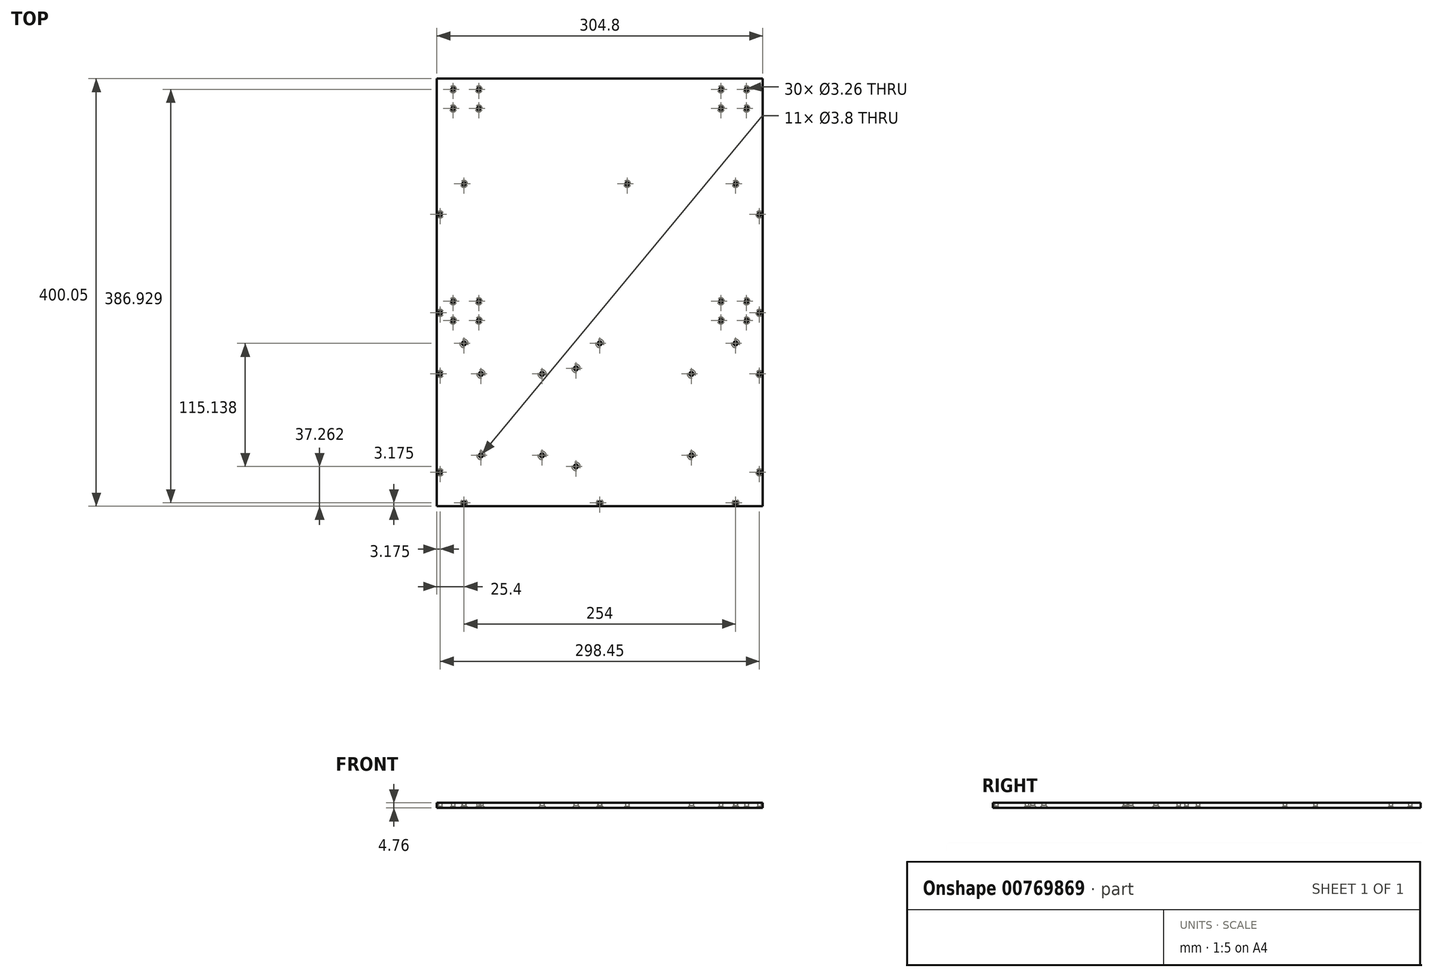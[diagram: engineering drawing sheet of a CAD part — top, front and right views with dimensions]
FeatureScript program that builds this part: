
annotation { "Feature Type Name" : "Feature", "Feature Type Description" : "" }
export const myFeature = defineFeature(function(context is Context, id is Id, definition is map)
    precondition{}
    {
        {
            var Q0;
            Q0=qCreatedBy(makeId("Top.planeOp"),FACE);
            var sketch = newSketch(context, id + "F0", { "sketchPlane" : qUnion([Q0])});
            skLineSegment(sketch, "E0.bottom", {"start": v(-152.4, 152.4) * mm, "end": v(152.4, 152.4) * mm});
            skLineSegment(sketch, "E0.top", {"start": v(-152.4, -152.4) * mm, "end": v(152.4, -152.4) * mm});
            skLineSegment(sketch, "E0.left", {"start": v(-152.4, 152.4) * mm, "end": v(-152.4, -152.4) * mm});
            skLineSegment(sketch, "E0.right", {"start": v(152.4, 152.4) * mm, "end": v(152.4, -152.4) * mm});
            skLineSegment(sketch, "E1", {"start": v(-152.4, 152.4) * mm, "end": v(152.4, -152.4) * mm, "construction": true});
            skSolve(sketch);
        }
        {
            var Q0;
            Q0 = qSketchRegion(id + "F0", true);
            extrude(context, id + "F1", {"entities" : qUnion([Q0]), "depth" : 4.76 * mm, "offsetDistance" : 25.4 * mm});
        }
        {
            var Q0;
            Q0=makeQuery(id+"F1.opExtrude","CAP_FACE",FACE,{"disambiguationData":[OSD([sQuery(id+"F0.wireOp",EDGE,"E0.bottom"),sQuery(id+"F0.wireOp",EDGE,"E0.top"),sQuery(id+"F0.wireOp",EDGE,"E0.left"),sQuery(id+"F0.wireOp",EDGE,"E0.right")])],"isStart":true});
            var sketch = newSketch(context, id + "F2", { "sketchPlane" : qUnion([Q0])});
            skLineSegment(sketch, "E2", {"start": v(-152.4, 0) * mm, "end": v(152.4, 0) * mm, "construction": true});
            skPoint(sketch, "E3", {"position": v(-127, 0) * mm});
            skPoint(sketch, "E4", {"position": v(0, 0) * mm});
            skPoint(sketch, "E5", {"position": v(127, 0) * mm});
            skSolve(sketch);
        }
        {
            var Q0;
            Q0=sQuery(id+"F2.wireOp",VERTEX,"E3");
            var Q1;
            Q1=sQuery(id+"F2.wireOp",VERTEX,"E4");
            var Q2;
            Q2=sQuery(id+"F2.wireOp",VERTEX,"E5");
            var Q3;
            Q3=makeQuery(id+"F1.opExtrude","SWEPT_BODY",BODY,{"disambiguationData":[OSD([sQuery(id+"F0.wireOp",EDGE,"E0.bottom"),sQuery(id+"F0.wireOp",EDGE,"E0.top"),sQuery(id+"F0.wireOp",EDGE,"E0.left"),sQuery(id+"F0.wireOp",EDGE,"E0.right")])]});
            hole(context, id + "F3", {"style" : HoleStyle.C_SINK, "endStyle" : HoleEndStyle.THROUGH, "standardTappedOrClearance" : lookupTablePath({ "standard" : "ANSI", "fit" : "Normal (ASME)", "size" : "#6", "type" : "Clearance" }), "standardBlindInLast" : lookupTablePath({ "fit" : "Free", "standard" : "ANSI", "size" : "#6", "type" : "Clearance" }), "holeDiameter" : 3.8 * mm, "cSinkDiameter" : 7.8 * mm, "cSinkAngle" : 82 * degree, "majorDiameter" : 6.35 * mm, "isTappedThrough" : true, "tappedDepth" : 7.77 * mm, "tapClearance" : 3, "locations" : qUnion([Q0, Q1, Q2]), "scope" : qUnion([Q3])});
        }
        {
            var Q0;
            Q0=makeQuery(id+"F1.opExtrude","CAP_FACE",FACE,{"disambiguationData":[OSD([sQuery(id+"F0.wireOp",EDGE,"E0.bottom"),sQuery(id+"F0.wireOp",EDGE,"E0.top"),sQuery(id+"F0.wireOp",EDGE,"E0.left"),sQuery(id+"F0.wireOp",EDGE,"E0.right")])],"isStart":false});
            var sketch = newSketch(context, id + "F4", { "sketchPlane" : qUnion([Q0])});
            skLineSegment(sketch, "E6.bottom", {"start": v(-152.4, 152.4) * mm, "end": v(152.4, 152.4) * mm});
            skLineSegment(sketch, "E6.top", {"start": v(-152.4, 247.65) * mm, "end": v(152.4, 247.65) * mm});
            skLineSegment(sketch, "E6.left", {"start": v(-152.4, 152.4) * mm, "end": v(-152.4, 247.65) * mm});
            skLineSegment(sketch, "E6.right", {"start": v(152.4, 152.4) * mm, "end": v(152.4, 247.65) * mm});
            skSolve(sketch);
        }
        {
            var Q0;
            Q0 = qSketchRegion(id + "F4", true);
            extrude(context, id + "F5", {"entities" : qUnion([Q0]), "operationType" : NewBodyOperationType.ADD, "oppositeDirection" : true, "depth" : 4.76 * mm, "offsetDistance" : 25.4 * mm});
        }
        {
            var Q0;
            Q0=makeQuery(id+"F5.boolean.opBoolean","MERGE",FACE,{"derivedFrom":[makeQuery(id+"F1.opExtrude","CAP_FACE",FACE,{"disambiguationData":[OSD([sQuery(id+"F0.wireOp",EDGE,"E0.bottom"),sQuery(id+"F0.wireOp",EDGE,"E0.top"),sQuery(id+"F0.wireOp",EDGE,"E0.left"),sQuery(id+"F0.wireOp",EDGE,"E0.right")])],"isStart":true}),makeQuery(id+"F5.opExtrude","CAP_FACE",FACE,{"disambiguationData":[OSD([sQuery(id+"F4.wireOp",EDGE,"E6.bottom"),sQuery(id+"F4.wireOp",EDGE,"E6.top"),sQuery(id+"F4.wireOp",EDGE,"E6.left"),sQuery(id+"F4.wireOp",EDGE,"E6.right")])],"isStart":false})]});
            var sketch = newSketch(context, id + "F6", { "sketchPlane" : qUnion([Q0])});
            skLineSegment(sketch, "E7", {"start": v(152.4, 149.23) * mm, "end": v(-152.4, 149.23) * mm, "construction": true});
            skPoint(sketch, "E8", {"position": v(127, 149.23) * mm});
            skPoint(sketch, "E9", {"position": v(0, 149.23) * mm});
            skPoint(sketch, "E10", {"position": v(-127, 149.23) * mm});
            skLineSegment(sketch, "E11", {"start": v(-152.4, -149.23) * mm, "end": v(152.4, -149.23) * mm, "construction": true});
            skPoint(sketch, "E12", {"position": v(-127, -149.23) * mm});
            skPoint(sketch, "E13", {"position": v(25.58, -149.23) * mm});
            skPoint(sketch, "E14", {"position": v(127, -149.23) * mm});
            skLineSegment(sketch, "E15", {"start": v(149.22, -247.65) * mm, "end": v(149.22, 152.4) * mm, "construction": true});
            skLineSegment(sketch, "E16", {"start": v(-149.22, -247.65) * mm, "end": v(-149.23, 152.4) * mm, "construction": true});
            skPoint(sketch, "E17", {"position": v(-149.23, -28.57) * mm});
            skPoint(sketch, "E18", {"position": v(-149.22, -120.65) * mm});
            skPoint(sketch, "E19", {"position": v(-149.23, 28.58) * mm});
            skPoint(sketch, "E20", {"position": v(-149.23, 120.65) * mm});
            skPoint(sketch, "E21", {"position": v(149.22, 120.65) * mm});
            skPoint(sketch, "E22", {"position": v(149.22, 28.58) * mm});
            skPoint(sketch, "E23", {"position": v(149.22, -28.57) * mm});
            skPoint(sketch, "E24", {"position": v(149.22, -120.65) * mm});
            skSolve(sketch);
        }
        {
            var Q0;
            Q0=sQuery(id+"F6.wireOp",VERTEX,"E8");
            var Q1;
            Q1=sQuery(id+"F6.wireOp",VERTEX,"E9");
            var Q2;
            Q2=sQuery(id+"F6.wireOp",VERTEX,"E10");
            var Q3;
            Q3=sQuery(id+"F6.wireOp",VERTEX,"E12");
            var Q4;
            Q4=sQuery(id+"F6.wireOp",VERTEX,"E13");
            var Q5;
            Q5=sQuery(id+"F6.wireOp",VERTEX,"E14");
            var Q6;
            Q6=sQuery(id+"F6.wireOp",VERTEX,"E24");
            var Q7;
            Q7=sQuery(id+"F6.wireOp",VERTEX,"E22");
            var Q8;
            Q8=sQuery(id+"F6.wireOp",VERTEX,"E21");
            var Q9;
            Q9=sQuery(id+"F6.wireOp",VERTEX,"E20");
            var Q10;
            Q10=sQuery(id+"F6.wireOp",VERTEX,"E19");
            var Q11;
            Q11=sQuery(id+"F6.wireOp",VERTEX,"E17");
            var Q12;
            Q12=sQuery(id+"F6.wireOp",VERTEX,"E18");
            var Q13;
            Q13=sQuery(id+"F6.wireOp",VERTEX,"E23");
            var Q14;
            Q14=makeQuery(id+"F1.opExtrude","SWEPT_BODY",BODY,{"disambiguationData":[OSD([sQuery(id+"F0.wireOp",EDGE,"E0.bottom"),sQuery(id+"F0.wireOp",EDGE,"E0.top"),sQuery(id+"F0.wireOp",EDGE,"E0.left"),sQuery(id+"F0.wireOp",EDGE,"E0.right")])]});
            hole(context, id + "F7", {"style" : HoleStyle.C_SINK, "endStyle" : HoleEndStyle.BLIND, "standardTappedOrClearance" : lookupTablePath({ "standard" : "ANSI", "fit" : "Normal (ASME)", "size" : "#4", "type" : "Clearance" }), "standardBlindInLast" : lookupTablePath({ "fit" : "Free", "standard" : "ANSI", "size" : "#4", "type" : "Clearance" }), "holeDiameter" : 3.26 * mm, "cSinkDiameter" : 6.48 * mm, "cSinkAngle" : 82 * degree, "majorDiameter" : 2.84 * mm, "holeDepth" : 13.74 * mm, "tappedDepth" : 11.84 * mm, "tapClearance" : 3, "locations" : qUnion([Q0, Q1, Q2, Q3, Q4, Q5, Q6, Q7, Q8, Q9, Q10, Q11, Q12, Q13]), "scope" : qUnion([Q14])});
        }
        {
            var Q0;
            Q0=makeQuery(id+"F5.boolean.opBoolean","MERGE",FACE,{"derivedFrom":[makeQuery(id+"F1.opExtrude","CAP_FACE",FACE,{"disambiguationData":[OSD([sQuery(id+"F0.wireOp",EDGE,"E0.bottom"),sQuery(id+"F0.wireOp",EDGE,"E0.top"),sQuery(id+"F0.wireOp",EDGE,"E0.left"),sQuery(id+"F0.wireOp",EDGE,"E0.right")])],"isStart":true}),makeQuery(id+"F5.opExtrude","CAP_FACE",FACE,{"disambiguationData":[OSD([sQuery(id+"F4.wireOp",EDGE,"E6.bottom"),sQuery(id+"F4.wireOp",EDGE,"E6.top"),sQuery(id+"F4.wireOp",EDGE,"E6.left"),sQuery(id+"F4.wireOp",EDGE,"E6.right")])],"isStart":false})]});
            var sketch = newSketch(context, id + "F8", { "sketchPlane" : qUnion([Q0])});
            skLineSegment(sketch, "E25.bottom", {"start": v(137.24, -237.7) * mm, "end": v(113.24, -237.7) * mm, "construction": true});
            skLineSegment(sketch, "E25.top", {"start": v(137.24, -219.7) * mm, "end": v(113.24, -219.7) * mm, "construction": true});
            skLineSegment(sketch, "E25.left", {"start": v(137.24, -237.7) * mm, "end": v(137.24, -219.7) * mm, "construction": true});
            skLineSegment(sketch, "E25.right", {"start": v(113.24, -237.7) * mm, "end": v(113.24, -219.7) * mm, "construction": true});
            skLineSegment(sketch, "E26.bottom", {"start": v(137.24, -39.36) * mm, "end": v(113.24, -39.36) * mm, "construction": true});
            skLineSegment(sketch, "E26.top", {"start": v(137.24, -21.36) * mm, "end": v(113.24, -21.36) * mm, "construction": true});
            skLineSegment(sketch, "E26.left", {"start": v(137.24, -39.36) * mm, "end": v(137.24, -21.36) * mm, "construction": true});
            skLineSegment(sketch, "E26.right", {"start": v(113.24, -39.36) * mm, "end": v(113.24, -21.36) * mm, "construction": true});
            skLineSegment(sketch, "E27.bottom", {"start": v(-113.23, -39.36) * mm, "end": v(-137.23, -39.36) * mm, "construction": true});
            skLineSegment(sketch, "E27.top", {"start": v(-113.23, -21.36) * mm, "end": v(-137.23, -21.36) * mm, "construction": true});
            skLineSegment(sketch, "E27.left", {"start": v(-113.23, -39.36) * mm, "end": v(-113.23, -21.36) * mm, "construction": true});
            skLineSegment(sketch, "E27.right", {"start": v(-137.23, -39.36) * mm, "end": v(-137.23, -21.36) * mm, "construction": true});
            skLineSegment(sketch, "E28.bottom", {"start": v(-113.23, -237.7) * mm, "end": v(-137.23, -237.7) * mm, "construction": true});
            skLineSegment(sketch, "E28.top", {"start": v(-113.23, -219.7) * mm, "end": v(-137.23, -219.7) * mm, "construction": true});
            skLineSegment(sketch, "E28.left", {"start": v(-113.23, -237.7) * mm, "end": v(-113.23, -219.7) * mm, "construction": true});
            skLineSegment(sketch, "E28.right", {"start": v(-137.23, -237.7) * mm, "end": v(-137.23, -219.7) * mm, "construction": true});
            skSolve(sketch);
        }
        {
            var Q0;
            Q0=sQuery(id+"F8.wireOp",VERTEX,"E27.top.end");
            var Q1;
            Q1=sQuery(id+"F8.wireOp",VERTEX,"E27.bottom.end");
            var Q2;
            Q2=sQuery(id+"F8.wireOp",VERTEX,"E27.bottom.start");
            var Q3;
            Q3=sQuery(id+"F8.wireOp",VERTEX,"E27.top.start");
            var Q4;
            Q4=sQuery(id+"F8.wireOp",VERTEX,"E28.top.start");
            var Q5;
            Q5=sQuery(id+"F8.wireOp",VERTEX,"E28.bottom.start");
            var Q6;
            Q6=sQuery(id+"F8.wireOp",VERTEX,"E28.bottom.end");
            var Q7;
            Q7=sQuery(id+"F8.wireOp",VERTEX,"E28.top.end");
            var Q8;
            Q8=sQuery(id+"F8.wireOp",VERTEX,"E25.bottom.end");
            var Q9;
            Q9=sQuery(id+"F8.wireOp",VERTEX,"E25.top.end");
            var Q10;
            Q10=sQuery(id+"F8.wireOp",VERTEX,"E25.top.start");
            var Q11;
            Q11=sQuery(id+"F8.wireOp",VERTEX,"E25.bottom.start");
            var Q12;
            Q12=sQuery(id+"F8.wireOp",VERTEX,"E26.top.start");
            var Q13;
            Q13=sQuery(id+"F8.wireOp",VERTEX,"E26.top.end");
            var Q14;
            Q14=sQuery(id+"F8.wireOp",VERTEX,"E26.bottom.end");
            var Q15;
            Q15=sQuery(id+"F8.wireOp",VERTEX,"E26.bottom.start");
            var Q16;
            Q16=makeQuery(id+"F1.opExtrude","SWEPT_BODY",BODY,{"disambiguationData":[OSD([sQuery(id+"F0.wireOp",EDGE,"E0.bottom"),sQuery(id+"F0.wireOp",EDGE,"E0.top"),sQuery(id+"F0.wireOp",EDGE,"E0.left"),sQuery(id+"F0.wireOp",EDGE,"E0.right")])]});
            hole(context, id + "F9", {"style" : HoleStyle.C_SINK, "endStyle" : HoleEndStyle.BLIND, "standardTappedOrClearance" : lookupTablePath({ "standard" : "ANSI", "fit" : "Normal (ASME)", "size" : "#4", "type" : "Clearance" }), "standardBlindInLast" : lookupTablePath({ "fit" : "Free", "standard" : "ANSI", "size" : "#4", "type" : "Clearance" }), "holeDiameter" : 3.26 * mm, "cSinkDiameter" : 6.48 * mm, "cSinkAngle" : 82 * degree, "majorDiameter" : 2.84 * mm, "holeDepth" : 13.74 * mm, "tappedDepth" : 11.84 * mm, "tapClearance" : 3, "locations" : qUnion([Q0, Q1, Q2, Q3, Q4, Q5, Q6, Q7, Q8, Q9, Q10, Q11, Q12, Q13, Q14, Q15]), "scope" : qUnion([Q16])});
        }
        {
            var Q0;
            Q0=makeQuery(id+"F5.boolean.opBoolean","MERGE",FACE,{"derivedFrom":[makeQuery(id+"F1.opExtrude","CAP_FACE",FACE,{"disambiguationData":[OSD([sQuery(id+"F0.wireOp",EDGE,"E0.bottom"),sQuery(id+"F0.wireOp",EDGE,"E0.top"),sQuery(id+"F0.wireOp",EDGE,"E0.left"),sQuery(id+"F0.wireOp",EDGE,"E0.right")])],"isStart":true}),makeQuery(id+"F5.opExtrude","CAP_FACE",FACE,{"disambiguationData":[OSD([sQuery(id+"F4.wireOp",EDGE,"E6.bottom"),sQuery(id+"F4.wireOp",EDGE,"E6.top"),sQuery(id+"F4.wireOp",EDGE,"E6.left"),sQuery(id+"F4.wireOp",EDGE,"E6.right")])],"isStart":false})]});
            var sketch = newSketch(context, id + "F10", { "sketchPlane" : qUnion([Q0])});
            skPoint(sketch, "E29", {"position": v(85.72, 28.57) * mm});
            skPoint(sketch, "E30", {"position": v(85.72, 104.77) * mm});
            skPoint(sketch, "E31", {"position": v(-22.23, 23.4) * mm});
            skPoint(sketch, "E32", {"position": v(-22.23, 115.14) * mm});
            skPoint(sketch, "E33", {"position": v(-53.98, 28.57) * mm});
            skPoint(sketch, "E34", {"position": v(-53.98, 104.77) * mm});
            skPoint(sketch, "E35", {"position": v(-111.13, 28.57) * mm});
            skPoint(sketch, "E36", {"position": v(-111.13, 104.77) * mm});
            skLineSegment(sketch, "E37", {"start": v(152.4, 0) * mm, "end": v(152.4, 152.4) * mm, "construction": true});
            skLineSegment(sketch, "E38", {"start": v(152.4, 152.4) * mm, "end": v(-152.4, 152.4) * mm, "construction": true});
            skLineSegment(sketch, "E39", {"start": v(-152.4, 152.4) * mm, "end": v(-152.4, 0) * mm, "construction": true});
            skSolve(sketch);
        }
        {
            var Q0;
            Q0=sQuery(id+"F10.wireOp",VERTEX,"E36");
            var Q1;
            Q1=sQuery(id+"F10.wireOp",VERTEX,"E35");
            var Q2;
            Q2=sQuery(id+"F10.wireOp",VERTEX,"E33");
            var Q3;
            Q3=sQuery(id+"F10.wireOp",VERTEX,"E34");
            var Q4;
            Q4=sQuery(id+"F10.wireOp",VERTEX,"E32");
            var Q5;
            Q5=sQuery(id+"F10.wireOp",VERTEX,"E31");
            var Q6;
            Q6=sQuery(id+"F10.wireOp",VERTEX,"E29");
            var Q7;
            Q7=sQuery(id+"F10.wireOp",VERTEX,"E30");
            var Q8;
            Q8=makeQuery(id+"F1.opExtrude","SWEPT_BODY",BODY,{"disambiguationData":[OSD([sQuery(id+"F0.wireOp",EDGE,"E0.bottom"),sQuery(id+"F0.wireOp",EDGE,"E0.top"),sQuery(id+"F0.wireOp",EDGE,"E0.left"),sQuery(id+"F0.wireOp",EDGE,"E0.right")])]});
            hole(context, id + "F11", {"style" : HoleStyle.C_SINK, "endStyle" : HoleEndStyle.THROUGH, "standardTappedOrClearance" : lookupTablePath({ "fit" : "Free", "standard" : "ANSI", "size" : "#6", "type" : "Clearance" }), "standardBlindInLast" : lookupTablePath({ "fit" : "Free", "standard" : "ANSI", "engagement" : "75%", "pitch" : "32 tpi", "size" : "#6", "type" : "Clearance & tapped" }), "holeDiameter" : 3.8 * mm, "cSinkDiameter" : 7.8 * mm, "cSinkAngle" : 82 * degree, "majorDiameter" : 6.35 * mm, "isTappedThrough" : true, "tappedDepth" : 7.77 * mm, "tapClearance" : 3, "locations" : qUnion([Q0, Q1, Q2, Q3, Q4, Q5, Q6, Q7]), "scope" : qUnion([Q8])});
        }
    });
